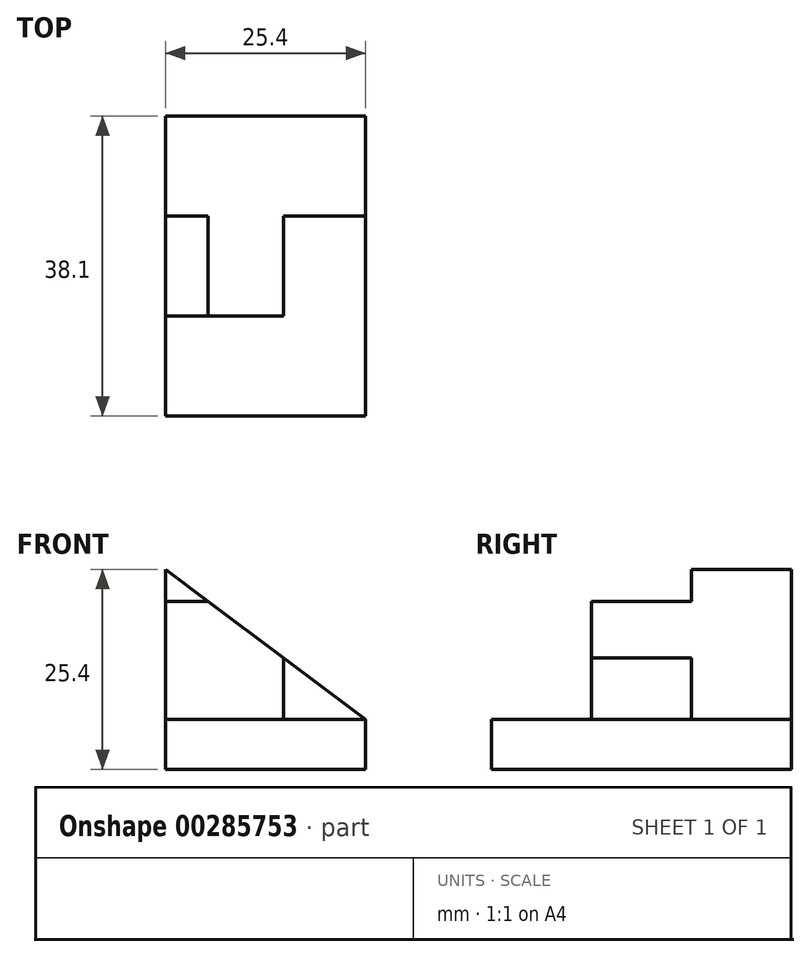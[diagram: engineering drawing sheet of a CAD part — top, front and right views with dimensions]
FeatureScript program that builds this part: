
annotation { "Feature Type Name" : "Feature", "Feature Type Description" : "" }
export const myFeature = defineFeature(function(context is Context, id is Id, definition is map)
    precondition{}
    {
        {
            var Q0;
            Q0=qCreatedBy(makeId("Top.planeOp"),FACE);
            var sketch = newSketch(context, id + "F0", { "sketchPlane" : qUnion([Q0])});
            skLineSegment(sketch, "E0.bottom", {"start": v(0, 0) * mm, "end": v(25.4, 0) * mm});
            skLineSegment(sketch, "E0.top", {"start": v(0, 38.1) * mm, "end": v(25.4, 38.1) * mm});
            skLineSegment(sketch, "E0.left", {"start": v(0, 0) * mm, "end": v(0, 38.1) * mm});
            skLineSegment(sketch, "E0.right", {"start": v(25.4, 0) * mm, "end": v(25.4, 38.1) * mm});
            skSolve(sketch);
        }
        {
            var Q0;
            Q0 = qSketchRegion(id + "F0", true);
            extrude(context, id + "F1", {"entities" : qUnion([Q0]), "oppositeDirection" : true, "depth" : 25.4 * mm});
        }
        {
            var Q0;
            Q0=qCreatedBy(makeId("Front.planeOp"),FACE);
            var sketch = newSketch(context, id + "F2", { "sketchPlane" : qUnion([Q0])});
            skLineSegment(sketch, "E1.bottom", {"start": v(0, 0) * mm, "end": v(25.4, 0) * mm});
            skLineSegment(sketch, "E1.top", {"start": v(0, -19.05) * mm, "end": v(25.4, -19.05) * mm});
            skLineSegment(sketch, "E1.left", {"start": v(0, 0) * mm, "end": v(0, -19.05) * mm});
            skLineSegment(sketch, "E1.right", {"start": v(25.4, 0) * mm, "end": v(25.4, -19.05) * mm});
            skSolve(sketch);
        }
        {
            var Q0;
            Q0 = qSketchRegion(id + "F2", true);
            extrude(context, id + "F3", {"entities" : qUnion([Q0]), "operationType" : NewBodyOperationType.REMOVE, "oppositeDirection" : true, "depth" : 12.7 * mm});
        }
        {
            var Q0;
            Q0=makeQuery(id+"F3.boolean.opBoolean","COPY",FACE,{"derivedFrom":makeQuery(id+"F3.opExtrude","CAP_FACE",FACE,{"disambiguationData":[OSD([sQuery(id+"F2.wireOp",EDGE,"E1.bottom"),sQuery(id+"F2.wireOp",EDGE,"E1.top"),sQuery(id+"F2.wireOp",EDGE,"E1.left"),sQuery(id+"F2.wireOp",EDGE,"E1.right")])],"isStart":false})});
            var sketch = newSketch(context, id + "F4", { "sketchPlane" : qUnion([Q0])});
            skLineSegment(sketch, "E2", {"start": v(0, 0) * mm, "end": v(25.4, -19.05) * mm});
            skLineSegment(sketch, "E3", {"start": v(0, 0) * mm, "end": v(25.4, 0) * mm});
            skLineSegment(sketch, "E4", {"start": v(25.4, 0) * mm, "end": v(25.4, -19.05) * mm});
            skSolve(sketch);
        }
        {
            var Q0;
            Q0=makeQuery(id+"F4.imprint","IMPRINT",FACE,{"disambiguationData":[TD([[makeQuery(id+"F4.imprint","IMPRINT",EDGE,{"derivedFrom":sQuery(id+"F4.wireOp",EDGE,"E2")}),1.0]])]});
            extrude(context, id + "F5", {"entities" : qUnion([Q0]), "operationType" : NewBodyOperationType.REMOVE, "oppositeDirection" : true, "depth" : 25.4 * mm});
        }
        {
            var Q0;
            Q0=qCreatedBy(makeId("Top.planeOp"),FACE);
            var sketch = newSketch(context, id + "F6", { "sketchPlane" : qUnion([Q0])});
            skLineSegment(sketch, "E5.bottom", {"start": v(0, 12.7) * mm, "end": v(25.4, 12.7) * mm});
            skLineSegment(sketch, "E5.top", {"start": v(0, 25.4) * mm, "end": v(25.4, 25.4) * mm});
            skLineSegment(sketch, "E5.left", {"start": v(0, 12.7) * mm, "end": v(0, 25.4) * mm});
            skLineSegment(sketch, "E5.right", {"start": v(25.4, 12.7) * mm, "end": v(25.4, 25.4) * mm});
            skSolve(sketch);
        }
        {
            var Q0;
            Q0 = qSketchRegion(id + "F6", true);
            extrude(context, id + "F7", {"entities" : qUnion([Q0]), "operationType" : NewBodyOperationType.ADD, "oppositeDirection" : true, "depth" : 25.4 * mm});
        }
        {
            var Q0;
            Q0=qCreatedBy(makeId("Front.planeOp"),FACE);
            var sketch = newSketch(context, id + "F8", { "sketchPlane" : qUnion([Q0])});
            skLineSegment(sketch, "E6.bottom", {"start": v(0, 0) * mm, "end": v(6.35, 0) * mm});
            skLineSegment(sketch, "E6.top", {"start": v(0, -4.06) * mm, "end": v(6.35, -4.06) * mm});
            skLineSegment(sketch, "E6.left", {"start": v(0, 0) * mm, "end": v(0, -4.06) * mm});
            skLineSegment(sketch, "E6.right", {"start": v(6.35, 0) * mm, "end": v(6.35, -4.06) * mm});
            skSolve(sketch);
        }
        {
            var Q0;
            Q0 = qSketchRegion(id + "F8", true);
            extrude(context, id + "F9", {"entities" : qUnion([Q0]), "operationType" : NewBodyOperationType.REMOVE, "oppositeDirection" : true, "depth" : 25.4 * mm});
        }
        {
            var Q0;
            Q0=qCreatedBy(makeId("Front.planeOp"),FACE);
            var sketch = newSketch(context, id + "F10", { "sketchPlane" : qUnion([Q0])});
            skLineSegment(sketch, "E7", {"start": v(0, 0) * mm, "end": v(15, -11.25) * mm});
            skLineSegment(sketch, "E8", {"start": v(15, -11.25) * mm, "end": v(15, 0) * mm});
            skLineSegment(sketch, "E9", {"start": v(15, 0) * mm, "end": v(0, 0) * mm});
            skLineSegment(sketch, "E10", {"start": v(15, 0) * mm, "end": v(27.7, 0) * mm});
            skLineSegment(sketch, "E11", {"start": v(27.7, 0) * mm, "end": v(27.7, -19.05) * mm});
            skLineSegment(sketch, "E12", {"start": v(27.7, -19.05) * mm, "end": v(15, -19.05) * mm});
            skLineSegment(sketch, "E13", {"start": v(15, -19.05) * mm, "end": v(15, 0) * mm});
            skSolve(sketch);
        }
        {
            var Q0;
            {var subQ3=sQuery(id+"F10.wireOp",EDGE,"E10");Q0=makeQuery(id+"F10.imprint","IMPRINT",FACE,{"disambiguationData":[TD([[makeQuery(id+"F10.imprint","IMPRINT",EDGE,{"derivedFrom":subQ3}),-1.0]])]});}
            var Q1;
            {var subQ0=sQuery(id+"F10.wireOp",EDGE,"E7");Q1=makeQuery(id+"F10.imprint","IMPRINT",FACE,{"disambiguationData":[TD([[makeQuery(id+"F10.imprint","IMPRINT",EDGE,{"derivedFrom":subQ0}),1.0]])]});}
            extrude(context, id + "F11", {"entities" : qUnion([Q0, Q1]), "operationType" : NewBodyOperationType.REMOVE, "oppositeDirection" : true, "depth" : 25.4 * mm});
        }
    });
